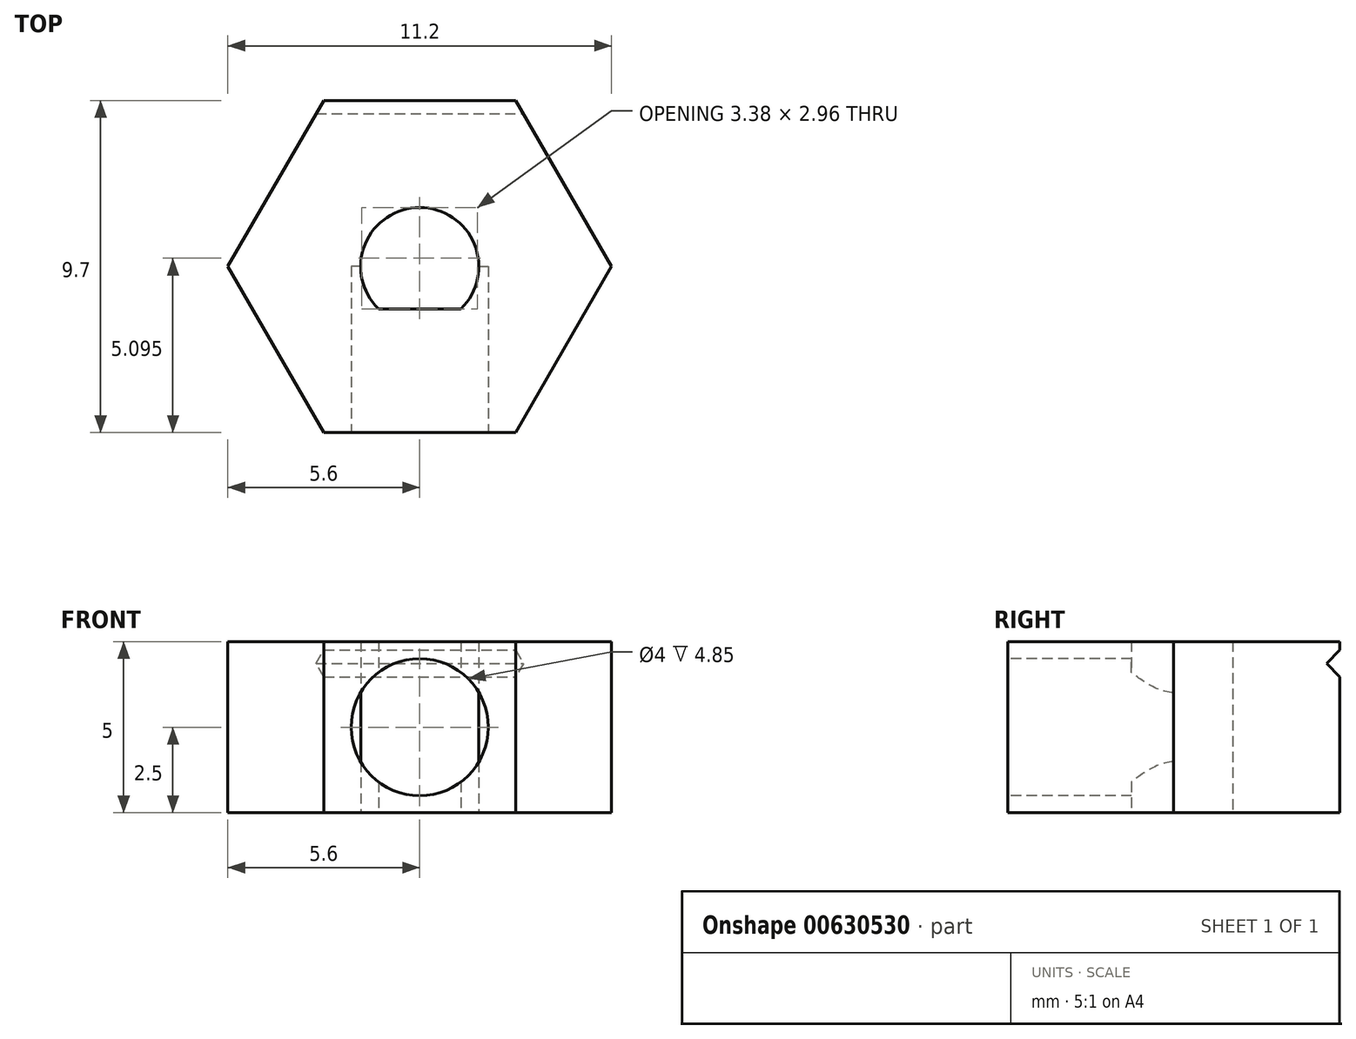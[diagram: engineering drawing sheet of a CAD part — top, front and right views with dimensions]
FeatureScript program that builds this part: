
annotation { "Feature Type Name" : "Feature", "Feature Type Description" : "" }
export const myFeature = defineFeature(function(context is Context, id is Id, definition is map)
    precondition{}
    {
        {
            var Q0;
            Q0=qCreatedBy(makeId("Top.planeOp"),FACE);
            var sketch = newSketch(context, id + "F0", { "sketchPlane" : qUnion([Q0])});
            skCircle(sketch, "E0.cCircle", {"center": v(0, 0) * mm, "radius": 4.85 * mm, "construction": true});
            skLineSegment(sketch, "E0.0", {"start": v(-5.6, 0) * mm, "end": v(-2.8, 4.85) * mm});
            skLineSegment(sketch, "E0.1", {"start": v(-2.8, 4.85) * mm, "end": v(2.8, 4.85) * mm});
            skLineSegment(sketch, "E0.2", {"start": v(2.8, 4.85) * mm, "end": v(5.6, 0) * mm});
            skLineSegment(sketch, "E0.3", {"start": v(5.6, 0) * mm, "end": v(2.8, -4.85) * mm});
            skLineSegment(sketch, "E0.4", {"start": v(2.8, -4.85) * mm, "end": v(-2.8, -4.85) * mm});
            skLineSegment(sketch, "E0.5", {"start": v(-2.8, -4.85) * mm, "end": v(-5.6, 0) * mm});
            skPoint(sketch, "E0.0.midPoint", {"position": v(-4.2, 2.43) * mm});
            skArc(sketch, "E1", {"start": v(1.2, -1.23) * mm, "mid": v(0, 1.72) * mm, "end": v(-1.2, -1.23) * mm});
            skLineSegment(sketch, "E2", {"start": v(-1.2, -1.23) * mm, "end": v(1.2, -1.23) * mm});
            skSolve(sketch);
        }
        {
            var Q0;
            Q0=makeQuery(id+"F0.imprint","IMPRINT",FACE,{"disambiguationData":[TD([[makeQuery(id+"F0.imprint","IMPRINT",EDGE,{"derivedFrom":sQuery(id+"F0.wireOp",EDGE,"E0.0")}),-1.0]])]});
            extrude(context, id + "F1", {"entities" : qUnion([Q0]), "depth" : 5 * mm, "offsetDistance" : 25 * mm});
        }
        {
            var Q0;
            Q0=qCreatedBy(makeId("Right.planeOp"),FACE);
            var sketch = newSketch(context, id + "F2", { "sketchPlane" : qUnion([Q0])});
            skLineSegment(sketch, "E3.0", {"start": v(4.85, 5) * mm, "end": v(4.85, 0) * mm});
            skLineSegment(sketch, "E4", {"start": v(4.85, 4.75) * mm, "end": v(4.46, 4.36) * mm});
            skLineSegment(sketch, "E5", {"start": v(4.46, 4.36) * mm, "end": v(4.85, 3.97) * mm});
            skSolve(sketch);
        }
        {
            var Q0;
            {var subQ0=sQuery(id+"F2.wireOp",EDGE,"E4");Q0=makeQuery(id+"F2.imprint","IMPRINT",FACE,{"disambiguationData":[TD([[makeQuery(id+"F2.imprint","IMPRINT",EDGE,{"derivedFrom":subQ0}),1.0]])]});}
            extrude(context, id + "F3", {"entities" : qUnion([Q0]), "operationType" : NewBodyOperationType.REMOVE, "endBound" : BoundingType.SYMMETRIC, "oppositeDirection" : true, "depth" : 25 * mm, "offsetDistance" : 25 * mm});
        }
        {
            var Q0;
            Q0=makeQuery(id+"F1.opExtrude","SWEPT_FACE",FACE,{"disambiguationData":[OSD([sQuery(id+"F0.wireOp",EDGE,"E0.4")])]});
            var sketch = newSketch(context, id + "F4", { "sketchPlane" : qUnion([Q0])});
            skArc(sketch, "E6", {"start": v(-1.15, 4.14) * mm, "mid": v(0, 0.5) * mm, "end": v(1.15, 4.14) * mm});
            skPoint(sketch, "E7", {"position": v(-2.8, 2.5) * mm});
            skLineSegment(sketch, "E8", {"start": v(0, 4.94) * mm, "end": v(-1.15, 4.14) * mm, "construction": true});
            skLineSegment(sketch, "E9.MirrorCS", {"start": v(0, 4.94) * mm, "end": v(1.15, 4.14) * mm, "construction": true});
            skArc(sketch, "E10", {"start": v(-1.15, 4.14) * mm, "mid": v(0, 4.5) * mm, "end": v(1.15, 4.14) * mm});
            skSolve(sketch);
        }
        {
            var Q0;
            Q0=makeQuery(id+"F4.imprint","IMPRINT",FACE,{"disambiguationData":[TD([[makeQuery(id+"F4.imprint","IMPRINT",EDGE,{"derivedFrom":sQuery(id+"F4.wireOp",EDGE,"E6")}),1.0]])]});
            var Q1;
            Q1=qCreatedBy(makeId("Front.planeOp"),FACE);
            extrude(context, id + "F5", {"entities" : qUnion([Q0]), "operationType" : NewBodyOperationType.REMOVE, "endBound" : BoundingType.UP_TO_SURFACE, "oppositeDirection" : true, "depth" : 25 * mm, "endBoundEntityFace" : qUnion([Q1]), "offsetDistance" : 25 * mm});
        }
    });
